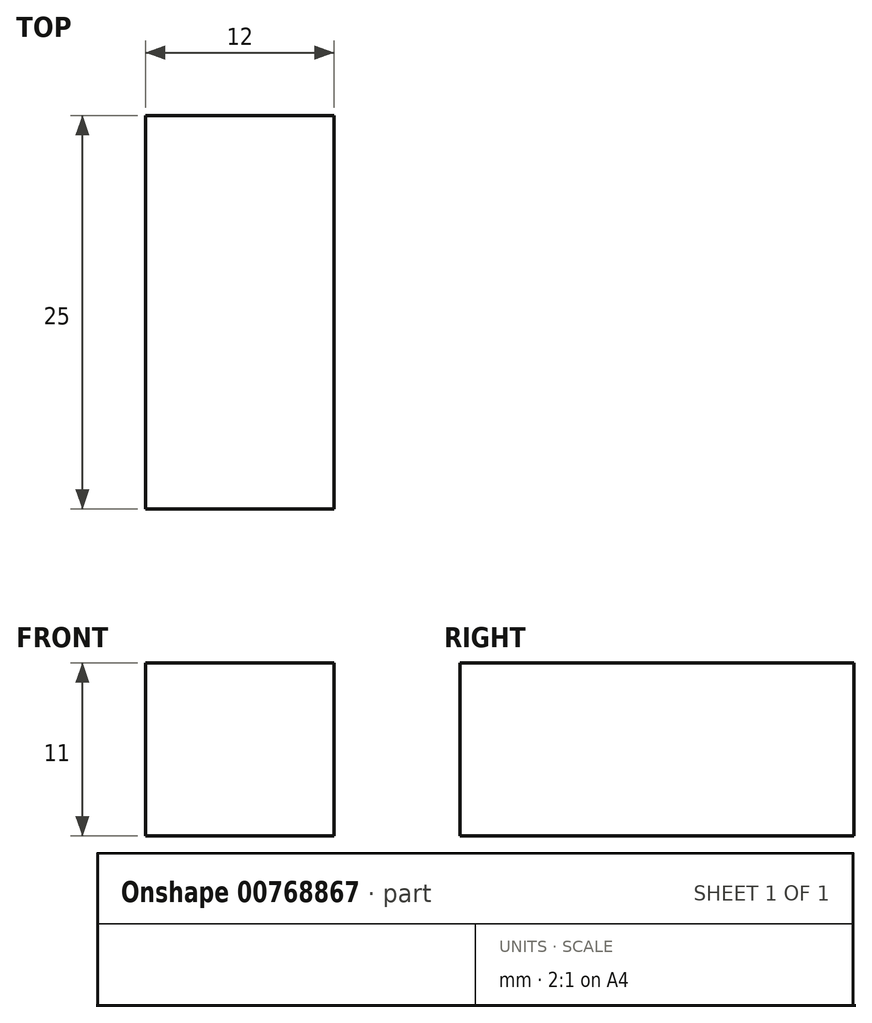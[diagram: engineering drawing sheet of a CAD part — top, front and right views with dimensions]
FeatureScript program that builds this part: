
annotation { "Feature Type Name" : "Feature", "Feature Type Description" : "" }
export const myFeature = defineFeature(function(context is Context, id is Id, definition is map)
    precondition{}
    {
        {
            var Q0;
            Q0=qCreatedBy(makeId("Front.planeOp"),FACE);
            var sketch = newSketch(context, id + "F0", { "sketchPlane" : qUnion([Q0])});
            skLineSegment(sketch, "E0.bottom", {"start": v(-6, 5.5) * mm, "end": v(6, 5.5) * mm});
            skLineSegment(sketch, "E0.top", {"start": v(-6, -5.5) * mm, "end": v(6, -5.5) * mm});
            skLineSegment(sketch, "E0.left", {"start": v(-6, 5.5) * mm, "end": v(-6, -5.5) * mm});
            skLineSegment(sketch, "E0.right", {"start": v(6, 5.5) * mm, "end": v(6, -5.5) * mm});
            skPoint(sketch, "E0.middle", {"position": v(0, 0) * mm});
            skSolve(sketch);
        }
        {
            var Q0;
            Q0 = qSketchRegion(id + "F0", true);
            extrude(context, id + "F1", {"entities" : qUnion([Q0]), "depth" : 25 * mm, "offsetDistance" : 25 * mm});
        }
    });
